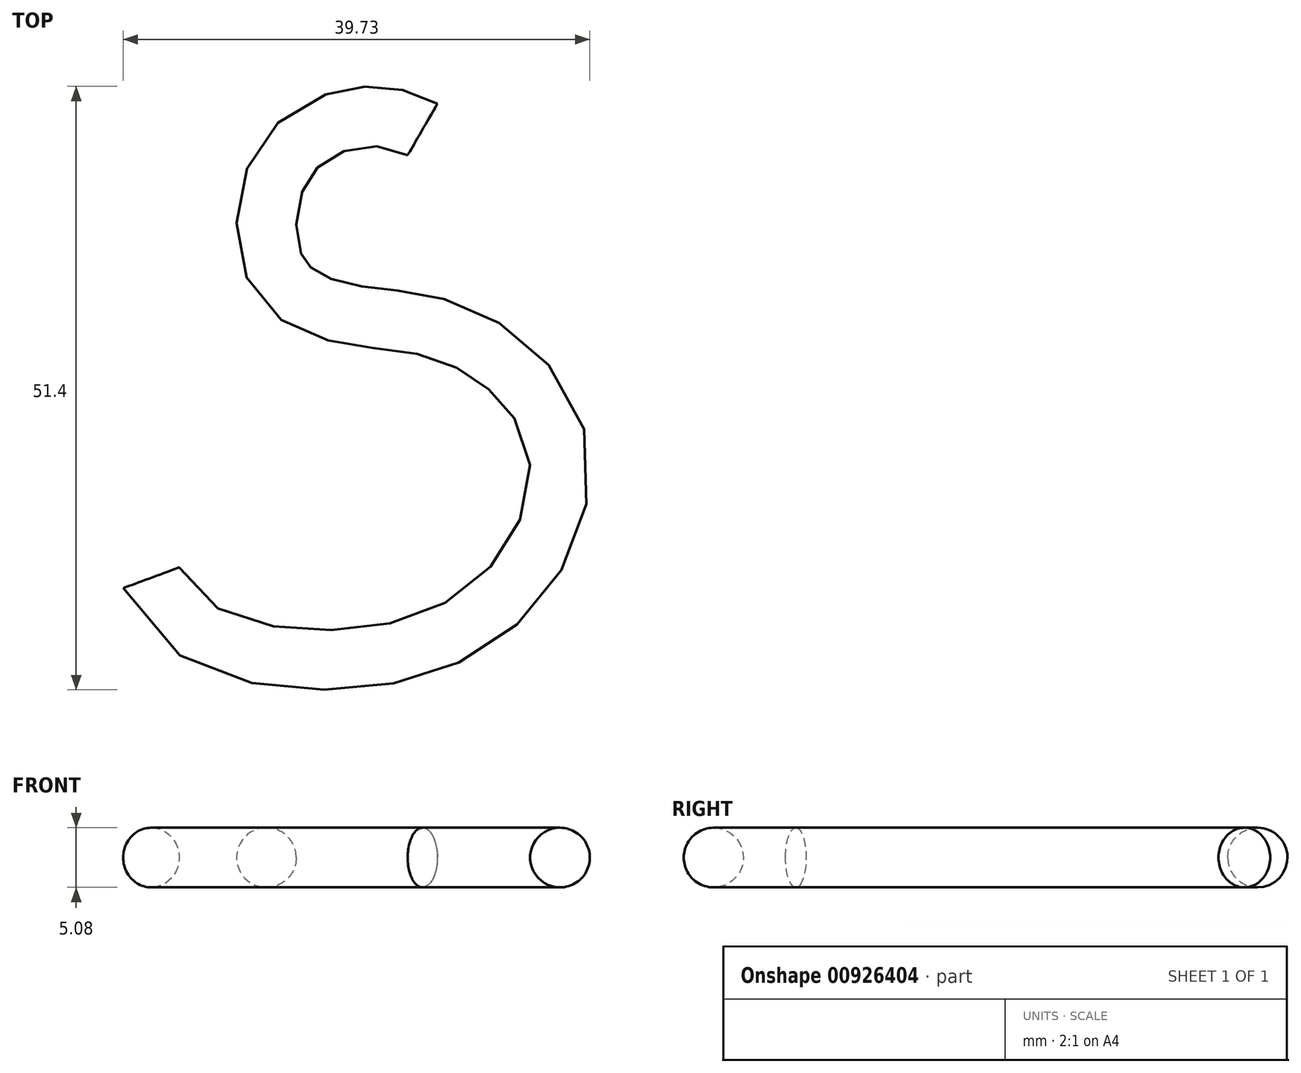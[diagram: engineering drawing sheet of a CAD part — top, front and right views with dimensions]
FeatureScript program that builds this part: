
annotation { "Feature Type Name" : "Feature", "Feature Type Description" : "" }
export const myFeature = defineFeature(function(context is Context, id is Id, definition is map)
    precondition{}
    {
        {
            var Q0;
            Q0=qCreatedBy(makeId("Top.planeOp"),FACE);
            var sketch = newSketch(context, id + "F0", { "sketchPlane" : qUnion([Q0])});
            skFitSpline(sketch, "E0", {"points": [v(-39.7, 50.53) * mm, v(-54.9, 47.56) * mm, v(-55.73, 33.86) * mm, v(-46.96, 29.22) * mm, v(-39.59, 27.92) * mm, v(-32.64, 21.04) * mm, v(-36.12, 10.5) * mm, v(-49.11, 5.73) * mm, v(-61.53, 10.83) * mm], "startDerivative": vector(-109.6, 63.2) * mm, "endDerivative": vector(-31.93, 86.62) * mm});
            skSolve(sketch);
        }
        {
            var Q0;
            Q0=sQuery(id+"F0.wireOp",VERTEX,"E0.start");
            var Q1;
            Q1=sQuery(id+"F0.wireOp",EDGE,"E0");
            cPlane(context, id + "F1", {"entities" : qUnion([Q0, Q1]), "cplaneType" : CPlaneType.CURVE_POINT, "offset" : 25.4 * mm, "width" : 152.4 * mm, "height" : 152.4 * mm});
        }
        {
            var Q0;
            Q0=qCreatedBy(id+"F1.planeOp",FACE);
            var sketch = newSketch(context, id + "F2", { "sketchPlane" : qUnion([Q0])});
            skCircle(sketch, "E1", {"center": v(-21.04, 0) * mm, "radius": 2.54 * mm});
            skSolve(sketch);
        }
        {
            var Q0;
            Q0=makeQuery(id+"F2.imprint","IMPRINT",FACE,{"disambiguationData":[TD([[makeQuery(id+"F2.imprint","IMPRINT",EDGE,{"derivedFrom":sQuery(id+"F2.wireOp",EDGE,"E1")}),1.0]])]});
            var Q1;
            Q1=sQuery(id+"F0.wireOp",EDGE,"E0");
            sweep(context, id + "F3", {"profiles" : qUnion([Q0]), "path" : qUnion([Q1])});
        }
    });
